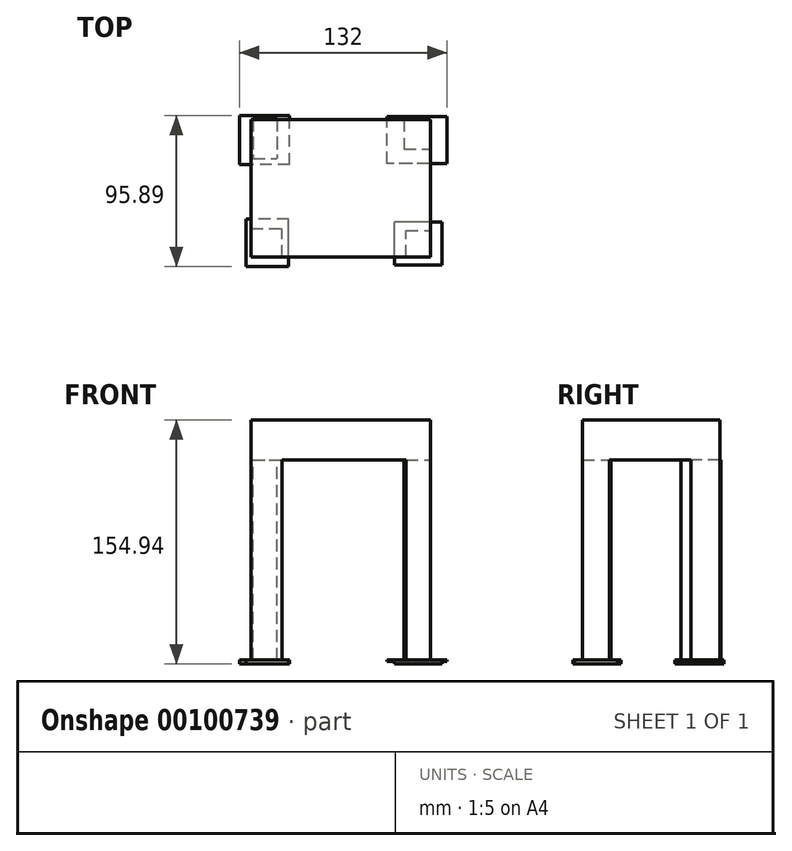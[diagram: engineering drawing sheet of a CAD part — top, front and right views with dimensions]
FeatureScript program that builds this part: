
annotation { "Feature Type Name" : "Feature", "Feature Type Description" : "" }
export const myFeature = defineFeature(function(context is Context, id is Id, definition is map)
    precondition{}
    {
        {
            var Q0;
            Q0=qCreatedBy(makeId("Top.planeOp"),FACE);
            var sketch = newSketch(context, id + "F0", { "sketchPlane" : qUnion([Q0])});
            skLineSegment(sketch, "E0.bottom", {"start": v(-57.47, 12.99) * mm, "end": v(56.4, 12.99) * mm});
            skLineSegment(sketch, "E0.top", {"start": v(-57.47, -23.38) * mm, "end": v(56.4, -23.38) * mm});
            skLineSegment(sketch, "E0.left", {"start": v(-57.47, 12.99) * mm, "end": v(-57.47, -23.38) * mm});
            skLineSegment(sketch, "E0.right", {"start": v(56.4, 12.99) * mm, "end": v(56.4, -23.38) * mm});
            skSolve(sketch);
        }
        {
            var Q0;
            Q0=makeQuery(id+"F0.imprint","IMPRINT",FACE,{"disambiguationData":[TD([[makeQuery(id+"F0.imprint","IMPRINT",EDGE,{"derivedFrom":sQuery(id+"F0.wireOp",EDGE,"E0.bottom")}),-1.0]])]});
            extrude(context, id + "F1", {"entities" : qUnion([Q0]), "depth" : 25.4 * mm});
        }
        {
            var Q0;
            Q0=makeQuery(id+"F1.opExtrude","SWEPT_FACE",FACE,{"disambiguationData":[OSD([sQuery(id+"F0.wireOp",EDGE,"E0.top")])]});
            extrude(context, id + "F2", {"entities" : qUnion([Q0]), "operationType" : NewBodyOperationType.ADD, "depth" : 50.8 * mm});
        }
        {
            var Q0;
            {var subQ0=sQuery(id+"F0.wireOp",EDGE,"E0.top");Q0=makeQuery(id+"F2.boolean.opBoolean","MERGE",FACE,{"derivedFrom":[makeQuery(id+"F1.opExtrude","CAP_FACE",FACE,{"disambiguationData":[OSD([sQuery(id+"F0.wireOp",EDGE,"E0.bottom"),subQ0,sQuery(id+"F0.wireOp",EDGE,"E0.left"),sQuery(id+"F0.wireOp",EDGE,"E0.right")])],"isStart":true}),makeQuery(id+"F2.opExtrude","SWEPT_FACE",FACE,{"disambiguationData":[OSD([subQ0]),TDD([makeQuery(id+"F1.opExtrude","CAP_EDGE",EDGE,{"disambiguationData":[OSD([subQ0])],"isStart":true})])]})]});}
            var sketch = newSketch(context, id + "F3", { "sketchPlane" : qUnion([Q0])});
            skLineSegment(sketch, "E1.bottom", {"start": v(41.09, 74.18) * mm, "end": v(56.4, 74.18) * mm});
            skLineSegment(sketch, "E1.top", {"start": v(41.09, 57.29) * mm, "end": v(56.4, 57.29) * mm});
            skLineSegment(sketch, "E1.left", {"start": v(41.09, 74.18) * mm, "end": v(41.09, 57.29) * mm});
            skLineSegment(sketch, "E1.right", {"start": v(56.4, 74.18) * mm, "end": v(56.4, 57.29) * mm});
            skSolve(sketch);
        }
        {
            var Q0;
            Q0 = qSketchRegion(id + "F3", true);
            extrude(context, id + "F4", {"entities" : qUnion([Q0]), "operationType" : NewBodyOperationType.ADD, "depth" : 127 * mm});
        }
        {
            var Q0;
            {var subQ0=sQuery(id+"F0.wireOp",EDGE,"E0.top");Q0=makeQuery(id+"F2.boolean.opBoolean","MERGE",FACE,{"derivedFrom":[makeQuery(id+"F1.opExtrude","CAP_FACE",FACE,{"disambiguationData":[OSD([sQuery(id+"F0.wireOp",EDGE,"E0.bottom"),subQ0,sQuery(id+"F0.wireOp",EDGE,"E0.left"),sQuery(id+"F0.wireOp",EDGE,"E0.right")])],"isStart":true}),makeQuery(id+"F2.opExtrude","SWEPT_FACE",FACE,{"disambiguationData":[OSD([subQ0]),TDD([makeQuery(id+"F1.opExtrude","CAP_EDGE",EDGE,{"disambiguationData":[OSD([subQ0])],"isStart":true})])]})]});}
            var sketch = newSketch(context, id + "F5", { "sketchPlane" : qUnion([Q0])});
            skLineSegment(sketch, "E2.bottom", {"start": v(-57.47, 74.18) * mm, "end": v(-37.67, 74.18) * mm});
            skLineSegment(sketch, "E2.top", {"start": v(-57.47, 56.11) * mm, "end": v(-37.67, 56.11) * mm});
            skLineSegment(sketch, "E2.left", {"start": v(-57.47, 74.18) * mm, "end": v(-57.47, 56.11) * mm});
            skLineSegment(sketch, "E2.right", {"start": v(-37.67, 74.18) * mm, "end": v(-37.67, 56.11) * mm});
            skSolve(sketch);
        }
        {
            var Q0;
            Q0 = qSketchRegion(id + "F5", true);
            extrude(context, id + "F6", {"entities" : qUnion([Q0]), "operationType" : NewBodyOperationType.ADD, "depth" : 127 * mm});
        }
        {
            var Q0;
            {var subQ0=sQuery(id+"F0.wireOp",EDGE,"E0.top");Q0=makeQuery(id+"F2.boolean.opBoolean","MERGE",FACE,{"derivedFrom":[makeQuery(id+"F1.opExtrude","CAP_FACE",FACE,{"disambiguationData":[OSD([sQuery(id+"F0.wireOp",EDGE,"E0.bottom"),subQ0,sQuery(id+"F0.wireOp",EDGE,"E0.left"),sQuery(id+"F0.wireOp",EDGE,"E0.right")])],"isStart":true}),makeQuery(id+"F2.opExtrude","SWEPT_FACE",FACE,{"disambiguationData":[OSD([subQ0]),TDD([makeQuery(id+"F1.opExtrude","CAP_EDGE",EDGE,{"disambiguationData":[OSD([subQ0])],"isStart":true})])]})]});}
            var sketch = newSketch(context, id + "F7", { "sketchPlane" : qUnion([Q0])});
            skLineSegment(sketch, "E3.bottom", {"start": v(39.63, -12.99) * mm, "end": v(56.4, -12.99) * mm});
            skLineSegment(sketch, "E3.top", {"start": v(39.63, 5.6) * mm, "end": v(56.4, 5.6) * mm});
            skLineSegment(sketch, "E3.left", {"start": v(39.63, -12.99) * mm, "end": v(39.63, 5.6) * mm});
            skLineSegment(sketch, "E3.right", {"start": v(56.4, -12.99) * mm, "end": v(56.4, 5.6) * mm});
            skSolve(sketch);
        }
        {
            var Q0;
            {var subQ4=sQuery(id+"F7.wireOp",EDGE,"E3.top");Q0=makeQuery(id+"F7.imprint","IMPRINT",FACE,{"disambiguationData":[TD([[makeQuery(id+"F7.imprint","IMPRINT",EDGE,{"derivedFrom":subQ4}),1.0]])]});}
            var sketch = newSketch(context, id + "F8", { "sketchPlane" : qUnion([Q0])});
            skSolve(sketch);
        }
        {
            var Q0;
            Q0=makeQuery(id+"F7.imprint","IMPRINT",FACE,{"disambiguationData":[TD([[makeQuery(id+"F7.imprint","IMPRINT",EDGE,{"derivedFrom":sQuery(id+"F7.wireOp",EDGE,"E3.bottom")}),1.0]])]});
            extrude(context, id + "F9", {"entities" : qUnion([Q0]), "operationType" : NewBodyOperationType.ADD, "depth" : 127 * mm});
        }
        {
            var Q0;
            {var subQ4=sQuery(id+"F7.wireOp",EDGE,"E3.top");Q0=makeQuery(id+"F8.imprint","IMPRINT",FACE,{"disambiguationData":[TD([[makeQuery(id+"F8.imprint","IMPRINT",EDGE,{"derivedFrom":makeQuery(id+"F7.imprint","IMPRINT",EDGE,{"derivedFrom":subQ4})}),1.0]])]});}
            var sketch = newSketch(context, id + "F10", { "sketchPlane" : qUnion([Q0])});
            skLineSegment(sketch, "E4.bottom", {"start": v(-56.19, -13.73) * mm, "end": v(-41.1, -13.73) * mm});
            skLineSegment(sketch, "E4.top", {"start": v(-56.19, 11.67) * mm, "end": v(-41.1, 11.67) * mm});
            skLineSegment(sketch, "E4.left", {"start": v(-56.19, -13.73) * mm, "end": v(-56.19, 11.67) * mm});
            skLineSegment(sketch, "E4.right", {"start": v(-41.1, -13.73) * mm, "end": v(-41.1, 11.67) * mm});
            skSolve(sketch);
        }
        {
            var Q0;
            Q0 = qSketchRegion(id + "F10", true);
            extrude(context, id + "F11", {"entities" : qUnion([Q0]), "operationType" : NewBodyOperationType.ADD, "depth" : 25.4 * mm});
        }
        {
            var Q0;
            Q0=makeQuery(id+"F11.opExtrude","CAP_FACE",FACE,{"disambiguationData":[OSD([sQuery(id+"F10.wireOp",EDGE,"E4.bottom"),sQuery(id+"F10.wireOp",EDGE,"E4.top"),sQuery(id+"F10.wireOp",EDGE,"E4.left"),sQuery(id+"F10.wireOp",EDGE,"E4.right")])],"isStart":false});
            var sketch = newSketch(context, id + "F12", { "sketchPlane" : qUnion([Q0])});
            skSolve(sketch);
        }
        {
            var Q0;
            Q0=makeQuery(id+"F12.imprint","IMPRINT",FACE,{"disambiguationData":[TD([[makeQuery(id+"F12.imprint","IMPRINT",EDGE,{"derivedFrom":makeQuery(id+"F11.opExtrude","CAP_EDGE",EDGE,{"disambiguationData":[OSD([sQuery(id+"F10.wireOp",EDGE,"E4.bottom")])],"isStart":false})}),1.0]])]});
            extrude(context, id + "F13", {"entities" : qUnion([Q0]), "operationType" : NewBodyOperationType.ADD, "depth" : 101.6 * mm});
        }
        {
            var Q0;
            Q0=makeQuery(id+"F13.opExtrude","CAP_FACE",FACE,{"disambiguationData":[OSD([sQuery(id+"F10.wireOp",EDGE,"E4.bottom"),sQuery(id+"F10.wireOp",EDGE,"E4.top"),sQuery(id+"F10.wireOp",EDGE,"E4.left"),sQuery(id+"F10.wireOp",EDGE,"E4.right")])],"isStart":false});
            var sketch = newSketch(context, id + "F14", { "sketchPlane" : qUnion([Q0])});
            skLineSegment(sketch, "E5.bottom", {"start": v(-32.93, 15.63) * mm, "end": v(-64.92, 15.63) * mm});
            skLineSegment(sketch, "E5.top", {"start": v(-32.93, -15.63) * mm, "end": v(-64.92, -15.63) * mm});
            skLineSegment(sketch, "E5.left", {"start": v(-32.93, 15.63) * mm, "end": v(-32.93, -15.63) * mm});
            skLineSegment(sketch, "E5.right", {"start": v(-64.92, 15.63) * mm, "end": v(-64.92, -15.63) * mm});
            skPoint(sketch, "E5.middle", {"position": v(-48.92, 0) * mm});
            skSolve(sketch);
        }
        {
            var Q0;
            Q0 = qSketchRegion(id + "F14", true);
            extrude(context, id + "F15", {"entities" : qUnion([Q0]), "operationType" : NewBodyOperationType.ADD, "depth" : 2.54 * mm});
        }
        {
            var Q0;
            Q0=makeQuery(id+"F6.opExtrude","CAP_FACE",FACE,{"disambiguationData":[OSD([sQuery(id+"F5.wireOp",EDGE,"E2.bottom"),sQuery(id+"F5.wireOp",EDGE,"E2.top"),sQuery(id+"F5.wireOp",EDGE,"E2.left"),sQuery(id+"F5.wireOp",EDGE,"E2.right")])],"isStart":false});
            var sketch = newSketch(context, id + "F16", { "sketchPlane" : qUnion([Q0])});
            skLineSegment(sketch, "E6.bottom", {"start": v(-33.59, 80.26) * mm, "end": v(-60.7, 80.26) * mm});
            skLineSegment(sketch, "E6.top", {"start": v(-33.59, 50.03) * mm, "end": v(-60.7, 50.03) * mm});
            skLineSegment(sketch, "E6.left", {"start": v(-33.59, 80.26) * mm, "end": v(-33.59, 50.03) * mm});
            skLineSegment(sketch, "E6.right", {"start": v(-60.7, 80.26) * mm, "end": v(-60.7, 50.03) * mm});
            skPoint(sketch, "E6.middle", {"position": v(-47.14, 65.14) * mm});
            skPoint(sketch, "E6.middle.positionSnap0", {"position": v(-37.67, 65.14) * mm});
            skPoint(sketch, "E6.centerSnap0", {"position": v(-37.67, 65.14) * mm});
            skSolve(sketch);
        }
        {
            var Q0;
            Q0 = qSketchRegion(id + "F16", true);
            extrude(context, id + "F17", {"entities" : qUnion([Q0]), "operationType" : NewBodyOperationType.ADD, "depth" : 2.54 * mm});
        }
        {
            var Q0;
            Q0=makeQuery(id+"F9.opExtrude","CAP_FACE",FACE,{"disambiguationData":[OSD([sQuery(id+"F7.wireOp",EDGE,"E3.bottom"),sQuery(id+"F7.wireOp",EDGE,"E3.top"),sQuery(id+"F7.wireOp",EDGE,"E3.left"),sQuery(id+"F7.wireOp",EDGE,"E3.right")])],"isStart":false});
            var sketch = newSketch(context, id + "F18", { "sketchPlane" : qUnion([Q0])});
            skLineSegment(sketch, "E7.bottom", {"start": v(67.08, 14.85) * mm, "end": v(28.96, 14.85) * mm});
            skLineSegment(sketch, "E7.top", {"start": v(67.08, -14.85) * mm, "end": v(28.96, -14.85) * mm});
            skLineSegment(sketch, "E7.left", {"start": v(67.08, 14.85) * mm, "end": v(67.08, -14.85) * mm});
            skLineSegment(sketch, "E7.right", {"start": v(28.96, 14.85) * mm, "end": v(28.96, -14.85) * mm});
            skPoint(sketch, "E7.middle", {"position": v(48.02, 0) * mm});
            skPoint(sketch, "E7.middle.positionSnap0", {"position": v(48.02, -12.99) * mm});
            skPoint(sketch, "E7.centerSnap0", {"position": v(48.02, -12.99) * mm});
            skSolve(sketch);
        }
        {
            var Q0;
            Q0 = qSketchRegion(id + "F18", true);
            extrude(context, id + "F19", {"entities" : qUnion([Q0]), "operationType" : NewBodyOperationType.ADD, "depth" : 1 * mm});
        }
        {
            var Q0;
            Q0=makeQuery(id+"F4.opExtrude","CAP_FACE",FACE,{"disambiguationData":[OSD([sQuery(id+"F3.wireOp",EDGE,"E1.bottom"),sQuery(id+"F3.wireOp",EDGE,"E1.top"),sQuery(id+"F3.wireOp",EDGE,"E1.left"),sQuery(id+"F3.wireOp",EDGE,"E1.right")])],"isStart":false});
            var sketch = newSketch(context, id + "F20", { "sketchPlane" : qUnion([Q0])});
            skLineSegment(sketch, "E8.bottom", {"start": v(63.88, 79.36) * mm, "end": v(33.58, 79.36) * mm});
            skLineSegment(sketch, "E8.top", {"start": v(63.88, 52.1) * mm, "end": v(33.58, 52.1) * mm});
            skLineSegment(sketch, "E8.left", {"start": v(63.88, 79.36) * mm, "end": v(63.88, 52.1) * mm});
            skLineSegment(sketch, "E8.right", {"start": v(33.58, 79.36) * mm, "end": v(33.58, 52.1) * mm});
            skPoint(sketch, "E8.middle", {"position": v(48.73, 65.73) * mm});
            skPoint(sketch, "E8.middle.positionSnap0", {"position": v(56.4, 65.73) * mm});
            skPoint(sketch, "E8.centerSnap0", {"position": v(56.4, 65.73) * mm});
            skSolve(sketch);
        }
        {
            var Q0;
            Q0 = qSketchRegion(id + "F20", true);
            extrude(context, id + "F21", {"entities" : qUnion([Q0]), "operationType" : NewBodyOperationType.ADD, "depth" : 2.54 * mm});
        }
    });
